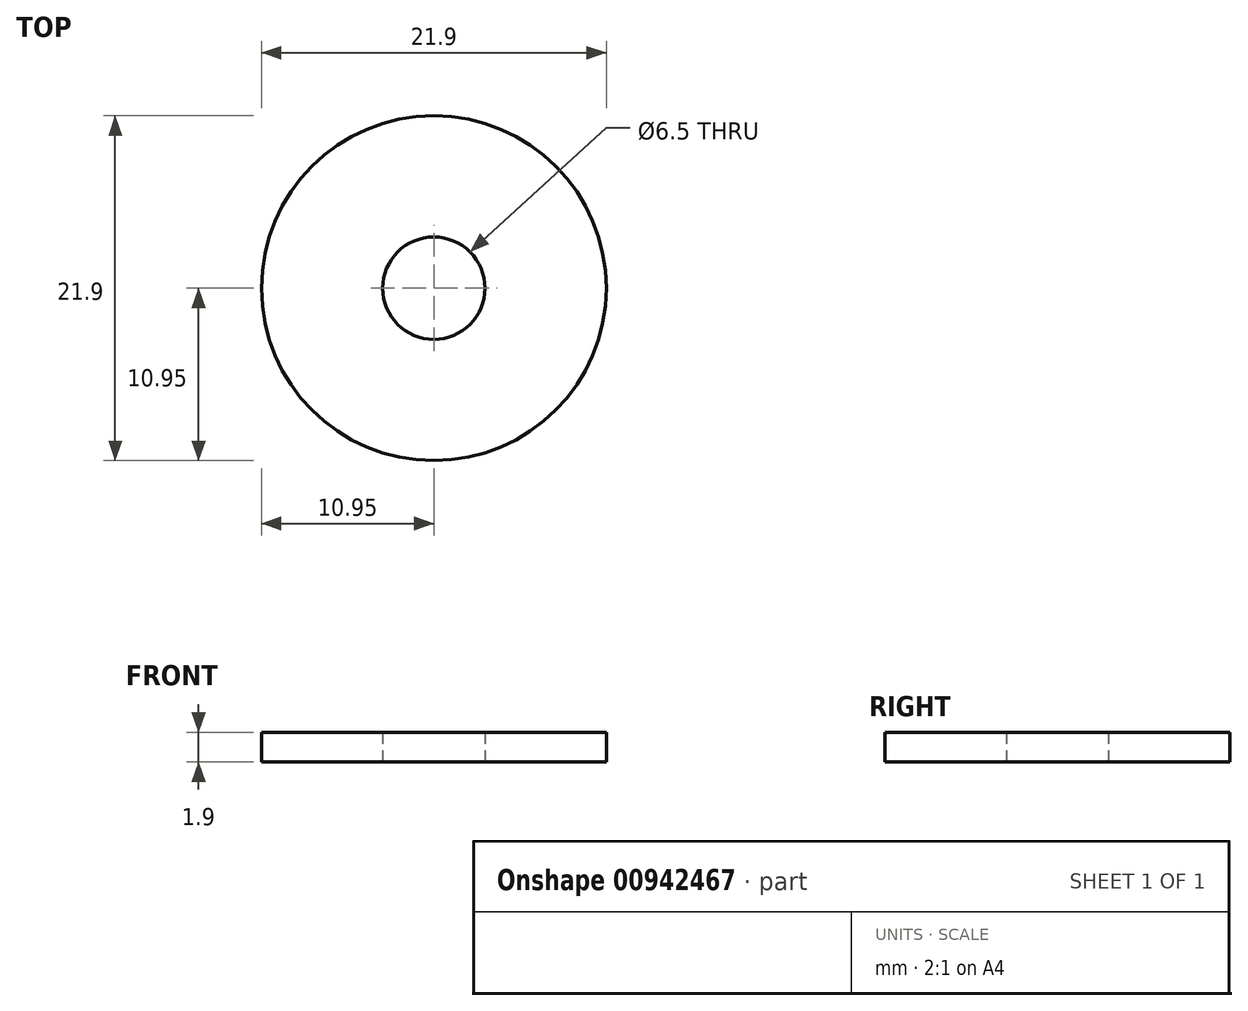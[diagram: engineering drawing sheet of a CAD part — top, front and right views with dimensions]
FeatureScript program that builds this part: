
annotation { "Feature Type Name" : "Feature", "Feature Type Description" : "" }
export const myFeature = defineFeature(function(context is Context, id is Id, definition is map)
    precondition{}
    {
        {
            var Q0;
            Q0=qCreatedBy(makeId("Top.planeOp"),FACE);
            var sketch = newSketch(context, id + "F0", { "sketchPlane" : qUnion([Q0])});
            skCircle(sketch, "E0", {"center": v(0, 0) * mm, "radius": 10.95 * mm});
            skCircle(sketch, "E1", {"center": v(0, 0) * mm, "radius": 3.25 * mm});
            skSolve(sketch);
        }
        {
            var Q0;
            Q0 = qSketchRegion(id + "F0", true);
            extrude(context, id + "F1", {"entities" : qUnion([Q0]), "depth" : 1.9 * mm, "offsetDistance" : 25 * mm});
        }
    });
